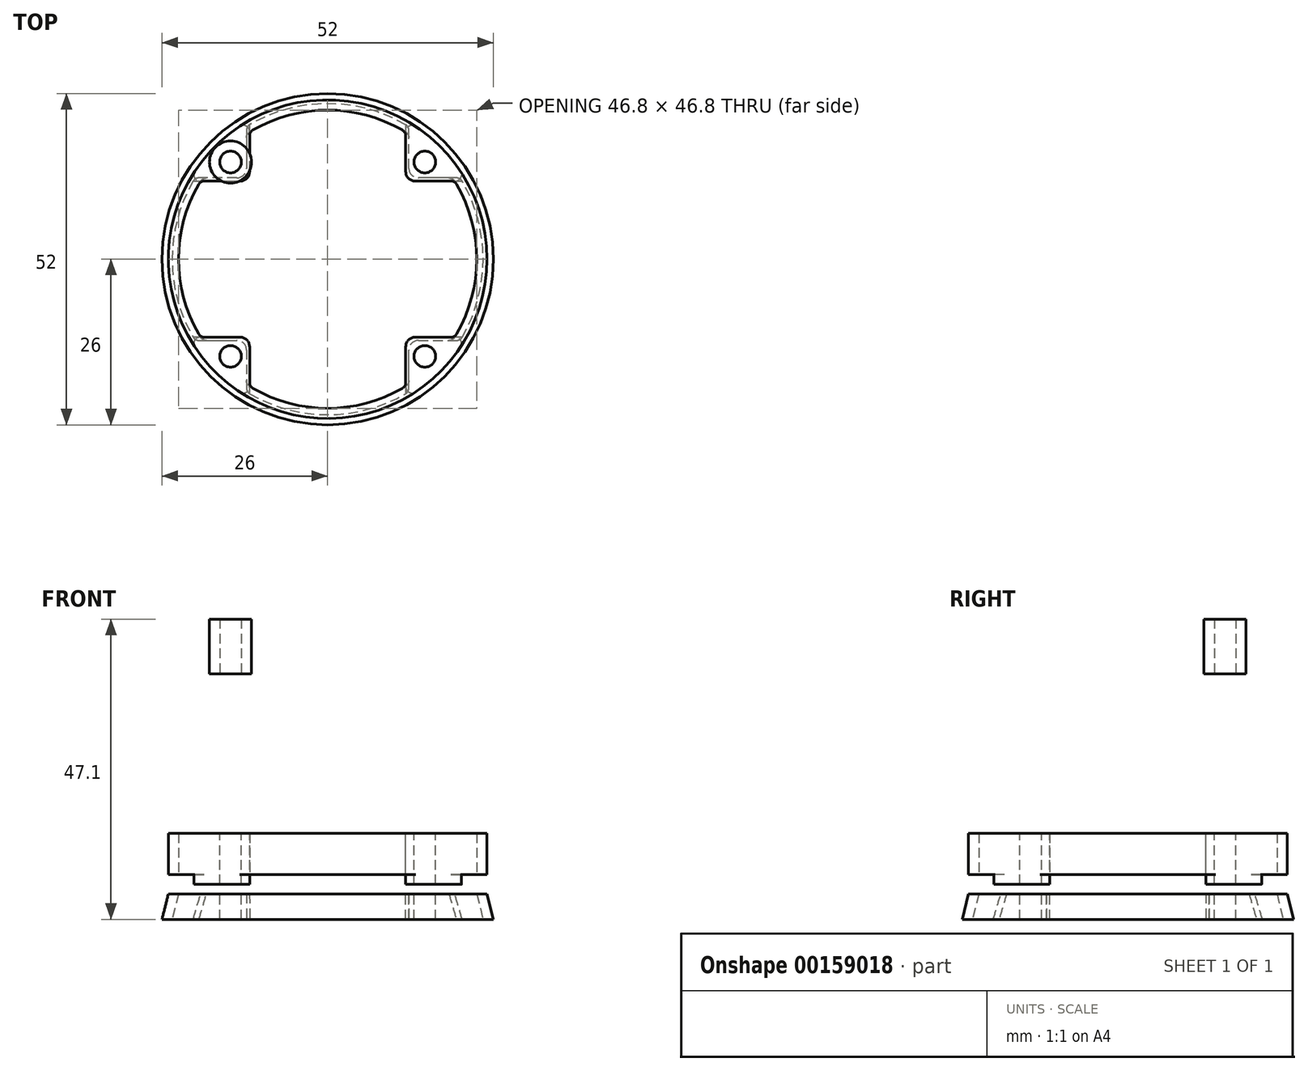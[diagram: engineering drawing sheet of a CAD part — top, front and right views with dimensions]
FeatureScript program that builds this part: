
annotation { "Feature Type Name" : "Feature", "Feature Type Description" : "" }
export const myFeature = defineFeature(function(context is Context, id is Id, definition is map)
    precondition{}
    {
        {
            var Q0;
            Q0=qCreatedBy(makeId("Top.planeOp"),FACE);
            var sketch = newSketch(context, id + "F0", { "sketchPlane" : qUnion([Q0])});
            skCircle(sketch, "E0", {"center": v(0, 0) * mm, "radius": 26 * mm});
            skLineSegment(sketch, "E1.bottom", {"start": v(-16.75, 17.75) * mm, "end": v(16.75, 17.75) * mm, "construction": true});
            skLineSegment(sketch, "E1.top", {"start": v(-16.75, -17.75) * mm, "end": v(16.75, -17.75) * mm, "construction": true});
            skLineSegment(sketch, "E1.left", {"start": v(-18.75, 15.75) * mm, "end": v(-18.75, -15.75) * mm, "construction": true});
            skLineSegment(sketch, "E1.right", {"start": v(18.75, 15.75) * mm, "end": v(18.75, -15.75) * mm, "construction": true});
            skPoint(sketch, "E2.visualSharp", {"position": v(-18.75, 17.75) * mm});
            skArc(sketch, "E2.filletArc", {"start": v(-16.75, 17.75) * mm, "mid": v(-18.16, 17.16) * mm, "end": v(-18.75, 15.75) * mm, "construction": true});
            skPoint(sketch, "E3.visualSharp", {"position": v(18.75, 17.75) * mm});
            skArc(sketch, "E3.filletArc", {"start": v(18.75, 15.75) * mm, "mid": v(18.16, 17.16) * mm, "end": v(16.75, 17.75) * mm, "construction": true});
            skPoint(sketch, "E4.visualSharp", {"position": v(18.75, -17.75) * mm});
            skArc(sketch, "E4.filletArc", {"start": v(16.75, -17.75) * mm, "mid": v(18.16, -17.16) * mm, "end": v(18.75, -15.75) * mm, "construction": true});
            skPoint(sketch, "E5.visualSharp", {"position": v(-18.75, -17.75) * mm});
            skArc(sketch, "E5.filletArc", {"start": v(-18.75, -15.75) * mm, "mid": v(-18.16, -17.16) * mm, "end": v(-16.75, -17.75) * mm, "construction": true});
            skSolve(sketch);
        }
        {
            var Q0;
            Q0 = qSketchRegion(id + "F0", true);
            extrude(context, id + "F1", {"entities" : qUnion([Q0]), "oppositeDirection" : true, "depth" : 4 * mm});
        }
        {
            var Q0;
            Q0=qCreatedBy(makeId("Front.planeOp"),FACE);
            var sketch = newSketch(context, id + "F2", { "sketchPlane" : qUnion([Q0])});
            skLineSegment(sketch, "E6", {"start": v(0, 0) * mm, "end": v(-23.4, 0) * mm});
            skLineSegment(sketch, "E7", {"start": v(-23.4, 0) * mm, "end": v(-24.9, -6) * mm});
            skLineSegment(sketch, "E8", {"start": v(-24.9, -6) * mm, "end": v(0, -6) * mm});
            skLineSegment(sketch, "E9", {"start": v(0, -6) * mm, "end": v(0, 0) * mm});
            skPoint(sketch, "E10", {"position": v(-24.4, -4) * mm});
            skPoint(sketch, "E11", {"position": v(0, -4) * mm});
            skLineSegment(sketch, "E12", {"start": v(0, 0) * mm, "end": v(0, -15.07) * mm, "construction": true});
            skPoint(sketch, "E12.endSnap0", {"position": v(0, -3) * mm});
            skSolve(sketch);
        }
        {
            var Q0;
            Q0 = qSketchRegion(id + "F2", true);
            var Q1;
            Q1=sQuery(id+"F2.wireOp",EDGE,"E12");
            revolve(context, id + "F3", {"operationType" : NewBodyOperationType.REMOVE, "entities" : qUnion([Q0]), "axis" : qUnion([Q1]), "revolveType" : RevolveType.FULL, "oppositeDirection" : true});
        }
        {
            var Q0;
            Q0=makeQuery(id+"F1.opExtrude","CAP_FACE",FACE,{"disambiguationData":[OSD([sQuery(id+"F0.wireOp",EDGE,"E0")])],"isStart":false});
            var sketch = newSketch(context, id + "F4", { "sketchPlane" : qUnion([Q0])});
            skLineSegment(sketch, "E13.bottom", {"start": v(-15.25, 15.25) * mm, "end": v(15.25, 15.25) * mm, "construction": true});
            skLineSegment(sketch, "E13.top", {"start": v(-15.25, -15.25) * mm, "end": v(15.25, -15.25) * mm, "construction": true});
            skLineSegment(sketch, "E13.left", {"start": v(-15.25, 15.25) * mm, "end": v(-15.25, -15.25) * mm, "construction": true});
            skLineSegment(sketch, "E13.right", {"start": v(15.25, 15.25) * mm, "end": v(15.25, -15.25) * mm, "construction": true});
            skPoint(sketch, "E13.middle", {"position": v(0, 0) * mm});
            skLineSegment(sketch, "E14", {"start": v(-20.8, 12.75) * mm, "end": v(-14.25, 12.75) * mm});
            skLineSegment(sketch, "E15", {"start": v(-12.75, 14.25) * mm, "end": v(-12.75, 20.8) * mm});
            skLineSegment(sketch, "E16", {"start": v(12.75, 20.8) * mm, "end": v(12.75, 14.25) * mm});
            skLineSegment(sketch, "E17", {"start": v(14.25, 12.75) * mm, "end": v(20.8, 12.75) * mm});
            skLineSegment(sketch, "E18", {"start": v(20.8, -12.75) * mm, "end": v(14.25, -12.75) * mm});
            skLineSegment(sketch, "E19", {"start": v(12.75, -14.25) * mm, "end": v(12.75, -20.8) * mm});
            skLineSegment(sketch, "E20", {"start": v(-12.75, -20.8) * mm, "end": v(-12.75, -14.25) * mm});
            skLineSegment(sketch, "E21", {"start": v(-14.25, -12.75) * mm, "end": v(-20.8, -12.75) * mm});
            skPoint(sketch, "E22.visualSharp", {"position": v(-12.75, 12.75) * mm});
            skArc(sketch, "E22.filletArc", {"start": v(-14.25, 12.75) * mm, "mid": v(-13.19, 13.19) * mm, "end": v(-12.75, 14.25) * mm});
            skPoint(sketch, "E23.visualSharp", {"position": v(12.75, 12.75) * mm});
            skArc(sketch, "E23.filletArc", {"start": v(12.75, 14.25) * mm, "mid": v(13.19, 13.19) * mm, "end": v(14.25, 12.75) * mm});
            skPoint(sketch, "E24.visualSharp", {"position": v(12.75, -12.75) * mm});
            skArc(sketch, "E24.filletArc", {"start": v(14.25, -12.75) * mm, "mid": v(13.19, -13.19) * mm, "end": v(12.75, -14.25) * mm});
            skPoint(sketch, "E25.visualSharp", {"position": v(-12.75, -12.75) * mm});
            skArc(sketch, "E25.filletArc", {"start": v(-12.75, -14.25) * mm, "mid": v(-13.19, -13.19) * mm, "end": v(-14.25, -12.75) * mm});
            skArc(sketch, "E26", {"start": v(-20.8, -12.75) * mm, "mid": v(-17.25, -17.25) * mm, "end": v(-12.75, -20.8) * mm});
            skArc(sketch, "E27.trimOffspring", {"start": v(-12.75, 20.8) * mm, "mid": v(-17.25, 17.25) * mm, "end": v(-20.8, 12.75) * mm});
            skArc(sketch, "E28.trimOffspring", {"start": v(20.8, 12.75) * mm, "mid": v(17.25, 17.25) * mm, "end": v(12.75, 20.8) * mm});
            skArc(sketch, "E29.trimOffspring", {"start": v(12.75, -20.8) * mm, "mid": v(17.25, -17.25) * mm, "end": v(20.8, -12.75) * mm});
            skSolve(sketch);
        }
        {
            var Q0;
            Q0 = qSketchRegion(id + "F4", true);
            var Q1;
            Q1=makeQuery(id+"F1.opExtrude","CAP_FACE",FACE,{"disambiguationData":[OSD([sQuery(id+"F0.wireOp",EDGE,"E0")])],"isStart":true});
            extrude(context, id + "F5", {"entities" : qUnion([Q0]), "operationType" : NewBodyOperationType.ADD, "endBound" : BoundingType.UP_TO_SURFACE, "oppositeDirection" : true, "endBoundEntityFace" : qUnion([Q1]), "depth" : 25 * mm});
        }
        {
            var Q0;
            {var subQ0=sQuery(id+"F0.wireOp",EDGE,"E0");Q0=makeQuery(id+"F5.boolean.opBoolean","MERGE",FACE,{"derivedFrom":[makeQuery(id+"F1.opExtrude","CAP_FACE",FACE,{"disambiguationData":[OSD([subQ0])],"isStart":true}),makeQuery(id+"F5.opExtrude","CAP_FACE",FACE,{"disambiguationData":[OSD([subQ0]),ownerDisambiguation([makeQuery(id+"F5.opExtrude","SWEPT_BODY",BODY,{"disambiguationData":[OSD([sQuery(id+"F4.wireOp",EDGE,"E14"),sQuery(id+"F4.wireOp",EDGE,"E15"),sQuery(id+"F4.wireOp",EDGE,"E22.filletArc"),sQuery(id+"F4.wireOp",EDGE,"E27.trimOffspring")])]})])],"isStart":false}),makeQuery(id+"F5.opExtrude","CAP_FACE",FACE,{"disambiguationData":[OSD([subQ0]),ownerDisambiguation([makeQuery(id+"F5.opExtrude","SWEPT_BODY",BODY,{"disambiguationData":[OSD([sQuery(id+"F4.wireOp",EDGE,"E16"),sQuery(id+"F4.wireOp",EDGE,"E17"),sQuery(id+"F4.wireOp",EDGE,"E23.filletArc"),sQuery(id+"F4.wireOp",EDGE,"E28.trimOffspring")])]})])],"isStart":false}),makeQuery(id+"F5.opExtrude","CAP_FACE",FACE,{"disambiguationData":[OSD([subQ0]),ownerDisambiguation([makeQuery(id+"F5.opExtrude","SWEPT_BODY",BODY,{"disambiguationData":[OSD([sQuery(id+"F4.wireOp",EDGE,"E18"),sQuery(id+"F4.wireOp",EDGE,"E19"),sQuery(id+"F4.wireOp",EDGE,"E24.filletArc"),sQuery(id+"F4.wireOp",EDGE,"E29.trimOffspring")])]})])],"isStart":false}),makeQuery(id+"F5.opExtrude","CAP_FACE",FACE,{"disambiguationData":[OSD([subQ0]),ownerDisambiguation([makeQuery(id+"F5.opExtrude","SWEPT_BODY",BODY,{"disambiguationData":[OSD([sQuery(id+"F4.wireOp",EDGE,"E20"),sQuery(id+"F4.wireOp",EDGE,"E21"),sQuery(id+"F4.wireOp",EDGE,"E25.filletArc"),sQuery(id+"F4.wireOp",EDGE,"E26")])]})])],"isStart":false})]});}
            var sketch = newSketch(context, id + "F6", { "sketchPlane" : qUnion([Q0])});
            skLineSegment(sketch, "E30.bottom", {"start": v(-15.25, 15.25) * mm, "end": v(15.25, 15.25) * mm, "construction": true});
            skLineSegment(sketch, "E30.top", {"start": v(-15.25, -15.25) * mm, "end": v(15.25, -15.25) * mm, "construction": true});
            skLineSegment(sketch, "E30.left", {"start": v(-15.25, 15.25) * mm, "end": v(-15.25, -15.25) * mm, "construction": true});
            skLineSegment(sketch, "E30.right", {"start": v(15.25, 15.25) * mm, "end": v(15.25, -15.25) * mm, "construction": true});
            skPoint(sketch, "E30.middle", {"position": v(0, 0) * mm});
            skCircle(sketch, "E31", {"center": v(-15.25, 15.25) * mm, "radius": 1.7 * mm});
            skCircle(sketch, "E32", {"center": v(15.25, 15.25) * mm, "radius": 1.7 * mm});
            skCircle(sketch, "E33", {"center": v(15.25, -15.25) * mm, "radius": 1.7 * mm});
            skCircle(sketch, "E34", {"center": v(-15.25, -15.25) * mm, "radius": 1.7 * mm});
            skSolve(sketch);
        }
        {
            var Q0;
            Q0 = qSketchRegion(id + "F6", true);
            extrude(context, id + "F7", {"entities" : qUnion([Q0]), "operationType" : NewBodyOperationType.REMOVE, "oppositeDirection" : true, "depth" : 25 * mm});
        }
        {
            var Q0;
            Q0=qCreatedBy(makeId("Front.planeOp"),FACE);
            var sketch = newSketch(context, id + "F8", { "sketchPlane" : qUnion([Q0])});
            skLineSegment(sketch, "E35", {"start": v(-26, -4) * mm, "end": v(-25, 0) * mm});
            skLineSegment(sketch, "E36", {"start": v(-25, 0) * mm, "end": v(-25, 4) * mm});
            skLineSegment(sketch, "E37", {"start": v(-25, 4) * mm, "end": v(-29.01, 4) * mm});
            skLineSegment(sketch, "E38", {"start": v(-29.01, 4) * mm, "end": v(-29.01, -4) * mm});
            skLineSegment(sketch, "E39", {"start": v(-29.01, -4) * mm, "end": v(-26, -4) * mm});
            skLineSegment(sketch, "E40", {"start": v(0, 0) * mm, "end": v(0, -9.03) * mm, "construction": true});
            skSolve(sketch);
        }
        {
            var Q0;
            Q0 = qSketchRegion(id + "F8", true);
            var Q1;
            Q1=sQuery(id+"F8.wireOp",EDGE,"E40");
            revolve(context, id + "F9", {"operationType" : NewBodyOperationType.REMOVE, "entities" : qUnion([Q0]), "axis" : qUnion([Q1]), "revolveType" : RevolveType.FULL, "oppositeDirection" : true});
        }
        {
            var Q0;
            Q0=makeQuery(id+"F5.boolean.opBoolean","INTERSECT",EDGE,{"derivedFrom":[makeQuery(id+"F3.boolean.opBoolean","COPY",FACE,{"derivedFrom":makeQuery(id+"F3.opRevolve","SWEPT_FACE",FACE,{"disambiguationData":[OSD([sQuery(id+"F2.wireOp",EDGE,"E7")])]})}),makeQuery(id+"F5.opExtrude","SWEPT_FACE",FACE,{"disambiguationData":[OSD([sQuery(id+"F4.wireOp",EDGE,"E21")])]})]});
            var Q1;
            Q1=makeQuery(id+"F5.boolean.opBoolean","INTERSECT",EDGE,{"derivedFrom":[makeQuery(id+"F3.boolean.opBoolean","COPY",FACE,{"derivedFrom":makeQuery(id+"F3.opRevolve","SWEPT_FACE",FACE,{"disambiguationData":[OSD([sQuery(id+"F2.wireOp",EDGE,"E7")])]})}),makeQuery(id+"F5.opExtrude","SWEPT_FACE",FACE,{"disambiguationData":[OSD([sQuery(id+"F4.wireOp",EDGE,"E14")])]})]});
            var Q2;
            Q2=makeQuery(id+"F5.boolean.opBoolean","INTERSECT",EDGE,{"derivedFrom":[makeQuery(id+"F3.boolean.opBoolean","COPY",FACE,{"derivedFrom":makeQuery(id+"F3.opRevolve","SWEPT_FACE",FACE,{"disambiguationData":[OSD([sQuery(id+"F2.wireOp",EDGE,"E7")])]})}),makeQuery(id+"F5.opExtrude","SWEPT_FACE",FACE,{"disambiguationData":[OSD([sQuery(id+"F4.wireOp",EDGE,"E15")])]})]});
            var Q3;
            Q3=makeQuery(id+"F5.boolean.opBoolean","INTERSECT",EDGE,{"derivedFrom":[makeQuery(id+"F3.boolean.opBoolean","COPY",FACE,{"derivedFrom":makeQuery(id+"F3.opRevolve","SWEPT_FACE",FACE,{"disambiguationData":[OSD([sQuery(id+"F2.wireOp",EDGE,"E7")])]})}),makeQuery(id+"F5.opExtrude","SWEPT_FACE",FACE,{"disambiguationData":[OSD([sQuery(id+"F4.wireOp",EDGE,"E16")])]})]});
            var Q4;
            Q4=makeQuery(id+"F5.boolean.opBoolean","INTERSECT",EDGE,{"derivedFrom":[makeQuery(id+"F3.boolean.opBoolean","COPY",FACE,{"derivedFrom":makeQuery(id+"F3.opRevolve","SWEPT_FACE",FACE,{"disambiguationData":[OSD([sQuery(id+"F2.wireOp",EDGE,"E7")])]})}),makeQuery(id+"F5.opExtrude","SWEPT_FACE",FACE,{"disambiguationData":[OSD([sQuery(id+"F4.wireOp",EDGE,"E17")])]})]});
            var Q5;
            Q5=makeQuery(id+"F5.boolean.opBoolean","INTERSECT",EDGE,{"derivedFrom":[makeQuery(id+"F3.boolean.opBoolean","COPY",FACE,{"derivedFrom":makeQuery(id+"F3.opRevolve","SWEPT_FACE",FACE,{"disambiguationData":[OSD([sQuery(id+"F2.wireOp",EDGE,"E7")])]})}),makeQuery(id+"F5.opExtrude","SWEPT_FACE",FACE,{"disambiguationData":[OSD([sQuery(id+"F4.wireOp",EDGE,"E18")])]})]});
            var Q6;
            Q6=makeQuery(id+"F5.boolean.opBoolean","INTERSECT",EDGE,{"derivedFrom":[makeQuery(id+"F3.boolean.opBoolean","COPY",FACE,{"derivedFrom":makeQuery(id+"F3.opRevolve","SWEPT_FACE",FACE,{"disambiguationData":[OSD([sQuery(id+"F2.wireOp",EDGE,"E7")])]})}),makeQuery(id+"F5.opExtrude","SWEPT_FACE",FACE,{"disambiguationData":[OSD([sQuery(id+"F4.wireOp",EDGE,"E19")])]})]});
            var Q7;
            Q7=makeQuery(id+"F5.boolean.opBoolean","INTERSECT",EDGE,{"derivedFrom":[makeQuery(id+"F3.boolean.opBoolean","COPY",FACE,{"derivedFrom":makeQuery(id+"F3.opRevolve","SWEPT_FACE",FACE,{"disambiguationData":[OSD([sQuery(id+"F2.wireOp",EDGE,"E7")])]})}),makeQuery(id+"F5.opExtrude","SWEPT_FACE",FACE,{"disambiguationData":[OSD([sQuery(id+"F4.wireOp",EDGE,"E20")])]})]});
            fillet(context, id + "F10", {"entities" : qUnion([Q0, Q1, Q2, Q3, Q4, Q5, Q6, Q7]), "radius" : 1 * mm, "tangentPropagation" : true, "allowEdgeOverflow" : false});
        }
        {
            var Q0;
            {var subQ0=sQuery(id+"F0.wireOp",EDGE,"E0");Q0=makeQuery(id+"F5.boolean.opBoolean","MERGE",FACE,{"derivedFrom":[makeQuery(id+"F1.opExtrude","CAP_FACE",FACE,{"disambiguationData":[OSD([subQ0])],"isStart":true}),makeQuery(id+"F5.opExtrude","CAP_FACE",FACE,{"disambiguationData":[OSD([subQ0]),ownerDisambiguation([makeQuery(id+"F5.opExtrude","SWEPT_BODY",BODY,{"disambiguationData":[OSD([sQuery(id+"F4.wireOp",EDGE,"E14"),sQuery(id+"F4.wireOp",EDGE,"E15"),sQuery(id+"F4.wireOp",EDGE,"E22.filletArc"),sQuery(id+"F4.wireOp",EDGE,"E27.trimOffspring")])]})])],"isStart":false}),makeQuery(id+"F5.opExtrude","CAP_FACE",FACE,{"disambiguationData":[OSD([subQ0]),ownerDisambiguation([makeQuery(id+"F5.opExtrude","SWEPT_BODY",BODY,{"disambiguationData":[OSD([sQuery(id+"F4.wireOp",EDGE,"E16"),sQuery(id+"F4.wireOp",EDGE,"E17"),sQuery(id+"F4.wireOp",EDGE,"E23.filletArc"),sQuery(id+"F4.wireOp",EDGE,"E28.trimOffspring")])]})])],"isStart":false}),makeQuery(id+"F5.opExtrude","CAP_FACE",FACE,{"disambiguationData":[OSD([subQ0]),ownerDisambiguation([makeQuery(id+"F5.opExtrude","SWEPT_BODY",BODY,{"disambiguationData":[OSD([sQuery(id+"F4.wireOp",EDGE,"E18"),sQuery(id+"F4.wireOp",EDGE,"E19"),sQuery(id+"F4.wireOp",EDGE,"E24.filletArc"),sQuery(id+"F4.wireOp",EDGE,"E29.trimOffspring")])]})])],"isStart":false}),makeQuery(id+"F5.opExtrude","CAP_FACE",FACE,{"disambiguationData":[OSD([subQ0]),ownerDisambiguation([makeQuery(id+"F5.opExtrude","SWEPT_BODY",BODY,{"disambiguationData":[OSD([sQuery(id+"F4.wireOp",EDGE,"E20"),sQuery(id+"F4.wireOp",EDGE,"E21"),sQuery(id+"F4.wireOp",EDGE,"E25.filletArc"),sQuery(id+"F4.wireOp",EDGE,"E26")])]})])],"isStart":false})]});}
            cPlane(context, id + "F11", {"entities" : qUnion([Q0]), "cplaneType" : CPlaneType.OFFSET, "offset" : 3 * mm, "width" : 150 * mm, "height" : 150 * mm});
        }
        {
            var Q0;
            Q0=qCreatedBy(id+"F11.planeOp",FACE);
            var sketch = newSketch(context, id + "F12", { "sketchPlane" : qUnion([Q0])});
            skCircle(sketch, "E41", {"center": v(0, 0) * mm, "radius": 25 * mm});
            skCircle(sketch, "E42", {"center": v(0, 0) * mm, "radius": 23.4 * mm});
            skSolve(sketch);
        }
        {
            var Q0;
            Q0 = qSketchRegion(id + "F12", true);
            extrude(context, id + "F13", {"entities" : qUnion([Q0]), "depth" : 6.5 * mm});
        }
        {
            var Q0;
            Q0=makeQuery(id+"F13.opExtrude","CAP_FACE",FACE,{"disambiguationData":[OSD([sQuery(id+"F12.wireOp",EDGE,"E41"),sQuery(id+"F12.wireOp",EDGE,"E42")])],"isStart":false});
            var sketch = newSketch(context, id + "F14", { "sketchPlane" : qUnion([Q0])});
            skArc(sketch, "E43", {"start": v(-21.8, -12.25) * mm, "mid": v(-17.68, -17.68) * mm, "end": v(-12.25, -21.8) * mm});
            skLineSegment(sketch, "E44", {"start": v(-21.8, 12.25) * mm, "end": v(-13.75, 12.25) * mm});
            skLineSegment(sketch, "E45", {"start": v(-12.25, 13.75) * mm, "end": v(-12.25, 21.8) * mm});
            skLineSegment(sketch, "E46", {"start": v(12.25, 21.8) * mm, "end": v(12.25, 13.75) * mm});
            skLineSegment(sketch, "E47", {"start": v(13.75, 12.25) * mm, "end": v(21.8, 12.25) * mm});
            skLineSegment(sketch, "E48", {"start": v(21.8, -12.25) * mm, "end": v(13.75, -12.25) * mm});
            skLineSegment(sketch, "E49", {"start": v(12.25, -13.75) * mm, "end": v(12.25, -21.8) * mm});
            skLineSegment(sketch, "E50", {"start": v(-21.8, -12.25) * mm, "end": v(-13.75, -12.25) * mm});
            skLineSegment(sketch, "E51", {"start": v(-12.25, -13.75) * mm, "end": v(-12.25, -21.8) * mm});
            skArc(sketch, "E52.trimOffspring", {"start": v(-12.25, 21.8) * mm, "mid": v(-17.68, 17.68) * mm, "end": v(-21.8, 12.25) * mm});
            skArc(sketch, "E53.trimOffspring", {"start": v(21.8, 12.25) * mm, "mid": v(17.68, 17.68) * mm, "end": v(12.25, 21.8) * mm});
            skArc(sketch, "E54.trimOffspring", {"start": v(12.25, -21.8) * mm, "mid": v(17.68, -17.68) * mm, "end": v(21.8, -12.25) * mm});
            skCircle(sketch, "E55.0", {"center": v(-15.25, 15.25) * mm, "radius": 1.7 * mm});
            skCircle(sketch, "E55.1", {"center": v(-15.25, -15.25) * mm, "radius": 1.7 * mm});
            skCircle(sketch, "E55.2", {"center": v(15.25, -15.25) * mm, "radius": 1.7 * mm});
            skCircle(sketch, "E55.3", {"center": v(15.25, 15.25) * mm, "radius": 1.7 * mm});
            skPoint(sketch, "E56.visualSharp", {"position": v(-12.25, 12.25) * mm});
            skArc(sketch, "E56.filletArc", {"start": v(-13.75, 12.25) * mm, "mid": v(-12.69, 12.69) * mm, "end": v(-12.25, 13.75) * mm});
            skPoint(sketch, "E57.visualSharp", {"position": v(12.25, 12.25) * mm});
            skArc(sketch, "E57.filletArc", {"start": v(12.25, 13.75) * mm, "mid": v(12.69, 12.69) * mm, "end": v(13.75, 12.25) * mm});
            skPoint(sketch, "E58.visualSharp", {"position": v(12.25, -12.25) * mm});
            skArc(sketch, "E58.filletArc", {"start": v(13.75, -12.25) * mm, "mid": v(12.69, -12.69) * mm, "end": v(12.25, -13.75) * mm});
            skPoint(sketch, "E59.visualSharp", {"position": v(-12.25, -12.25) * mm});
            skArc(sketch, "E59.filletArc", {"start": v(-12.25, -13.75) * mm, "mid": v(-12.69, -12.69) * mm, "end": v(-13.75, -12.25) * mm});
            skSolve(sketch);
        }
        {
            var Q0;
            Q0 = qSketchRegion(id + "F14", true);
            extrude(context, id + "F15", {"entities" : qUnion([Q0]), "operationType" : NewBodyOperationType.ADD, "oppositeDirection" : true, "depth" : 8 * mm});
        }
        {
            var Q0;
            Q0=makeQuery(id+"F15.boolean.opBoolean","INTERSECT",EDGE,{"derivedFrom":[makeQuery(id+"F13.opExtrude","SWEPT_FACE",FACE,{"disambiguationData":[OSD([sQuery(id+"F12.wireOp",EDGE,"E42")])]}),makeQuery(id+"F15.opExtrude","SWEPT_FACE",FACE,{"disambiguationData":[OSD([sQuery(id+"F14.wireOp",EDGE,"E44")])]})]});
            var Q1;
            Q1=makeQuery(id+"F15.boolean.opBoolean","INTERSECT",EDGE,{"derivedFrom":[makeQuery(id+"F13.opExtrude","SWEPT_FACE",FACE,{"disambiguationData":[OSD([sQuery(id+"F12.wireOp",EDGE,"E42")])]}),makeQuery(id+"F15.opExtrude","SWEPT_FACE",FACE,{"disambiguationData":[OSD([sQuery(id+"F14.wireOp",EDGE,"E45")])]})]});
            var Q2;
            Q2=makeQuery(id+"F15.boolean.opBoolean","INTERSECT",EDGE,{"derivedFrom":[makeQuery(id+"F13.opExtrude","SWEPT_FACE",FACE,{"disambiguationData":[OSD([sQuery(id+"F12.wireOp",EDGE,"E42")])]}),makeQuery(id+"F15.opExtrude","SWEPT_FACE",FACE,{"disambiguationData":[OSD([sQuery(id+"F14.wireOp",EDGE,"E46")])]})]});
            var Q3;
            Q3=makeQuery(id+"F15.boolean.opBoolean","INTERSECT",EDGE,{"derivedFrom":[makeQuery(id+"F13.opExtrude","SWEPT_FACE",FACE,{"disambiguationData":[OSD([sQuery(id+"F12.wireOp",EDGE,"E42")])]}),makeQuery(id+"F15.opExtrude","SWEPT_FACE",FACE,{"disambiguationData":[OSD([sQuery(id+"F14.wireOp",EDGE,"E47")])]})]});
            var Q4;
            Q4=makeQuery(id+"F15.boolean.opBoolean","INTERSECT",EDGE,{"derivedFrom":[makeQuery(id+"F13.opExtrude","SWEPT_FACE",FACE,{"disambiguationData":[OSD([sQuery(id+"F12.wireOp",EDGE,"E42")])]}),makeQuery(id+"F15.opExtrude","SWEPT_FACE",FACE,{"disambiguationData":[OSD([sQuery(id+"F14.wireOp",EDGE,"E48")])]})]});
            var Q5;
            Q5=makeQuery(id+"F15.boolean.opBoolean","INTERSECT",EDGE,{"derivedFrom":[makeQuery(id+"F13.opExtrude","SWEPT_FACE",FACE,{"disambiguationData":[OSD([sQuery(id+"F12.wireOp",EDGE,"E42")])]}),makeQuery(id+"F15.opExtrude","SWEPT_FACE",FACE,{"disambiguationData":[OSD([sQuery(id+"F14.wireOp",EDGE,"E49")])]})]});
            var Q6;
            Q6=makeQuery(id+"F15.boolean.opBoolean","INTERSECT",EDGE,{"derivedFrom":[makeQuery(id+"F13.opExtrude","SWEPT_FACE",FACE,{"disambiguationData":[OSD([sQuery(id+"F12.wireOp",EDGE,"E42")])]}),makeQuery(id+"F15.opExtrude","SWEPT_FACE",FACE,{"disambiguationData":[OSD([sQuery(id+"F14.wireOp",EDGE,"E51")])]})]});
            var Q7;
            Q7=makeQuery(id+"F15.boolean.opBoolean","INTERSECT",EDGE,{"derivedFrom":[makeQuery(id+"F13.opExtrude","SWEPT_FACE",FACE,{"disambiguationData":[OSD([sQuery(id+"F12.wireOp",EDGE,"E42")])]}),makeQuery(id+"F15.opExtrude","SWEPT_FACE",FACE,{"disambiguationData":[OSD([sQuery(id+"F14.wireOp",EDGE,"E50")])]})]});
            var Q8;
            Q8=makeQuery(id+"F15.opExtrude","SWEPT_EDGE",EDGE,{"disambiguationData":[OSD([sQuery(id+"F12.wireOp",EDGE,"E41"),sQuery(id+"F14.wireOp",EDGE,"E43"),sQuery(id+"F14.wireOp",EDGE,"E50")])]});
            var Q9;
            Q9=makeQuery(id+"F15.opExtrude","SWEPT_EDGE",EDGE,{"disambiguationData":[OSD([sQuery(id+"F12.wireOp",EDGE,"E41"),sQuery(id+"F14.wireOp",EDGE,"E44"),sQuery(id+"F14.wireOp",EDGE,"E52.trimOffspring")])]});
            var Q10;
            Q10=makeQuery(id+"F15.opExtrude","SWEPT_EDGE",EDGE,{"disambiguationData":[OSD([sQuery(id+"F12.wireOp",EDGE,"E41"),sQuery(id+"F14.wireOp",EDGE,"E43"),sQuery(id+"F14.wireOp",EDGE,"E51")])]});
            var Q11;
            Q11=makeQuery(id+"F15.opExtrude","SWEPT_EDGE",EDGE,{"disambiguationData":[OSD([sQuery(id+"F12.wireOp",EDGE,"E41"),sQuery(id+"F14.wireOp",EDGE,"E49"),sQuery(id+"F14.wireOp",EDGE,"E54.trimOffspring")])]});
            var Q12;
            Q12=makeQuery(id+"F15.opExtrude","SWEPT_EDGE",EDGE,{"disambiguationData":[OSD([sQuery(id+"F12.wireOp",EDGE,"E41"),sQuery(id+"F14.wireOp",EDGE,"E48"),sQuery(id+"F14.wireOp",EDGE,"E54.trimOffspring")])]});
            var Q13;
            Q13=makeQuery(id+"F15.opExtrude","SWEPT_EDGE",EDGE,{"disambiguationData":[OSD([sQuery(id+"F12.wireOp",EDGE,"E41"),sQuery(id+"F14.wireOp",EDGE,"E47"),sQuery(id+"F14.wireOp",EDGE,"E53.trimOffspring")])]});
            var Q14;
            Q14=makeQuery(id+"F15.opExtrude","SWEPT_EDGE",EDGE,{"disambiguationData":[OSD([sQuery(id+"F12.wireOp",EDGE,"E41"),sQuery(id+"F14.wireOp",EDGE,"E46"),sQuery(id+"F14.wireOp",EDGE,"E53.trimOffspring")])]});
            var Q15;
            Q15=makeQuery(id+"F15.opExtrude","SWEPT_EDGE",EDGE,{"disambiguationData":[OSD([sQuery(id+"F12.wireOp",EDGE,"E41"),sQuery(id+"F14.wireOp",EDGE,"E45"),sQuery(id+"F14.wireOp",EDGE,"E52.trimOffspring")])]});
            fillet(context, id + "F16", {"entities" : qUnion([Q0, Q1, Q2, Q3, Q4, Q5, Q6, Q7, Q8, Q9, Q10, Q11, Q12, Q13, Q14, Q15]), "radius" : 1 * mm, "tangentPropagation" : true, "allowEdgeOverflow" : false});
        }
        {
            var Q0;
            Q0=makeQuery(id+"F15.boolean.opBoolean","MERGE",FACE,{"derivedFrom":[makeQuery(id+"F13.opExtrude","CAP_FACE",FACE,{"disambiguationData":[OSD([sQuery(id+"F12.wireOp",EDGE,"E41"),sQuery(id+"F12.wireOp",EDGE,"E42")])],"isStart":false}),makeQuery(id+"F15.opExtrude","CAP_FACE",FACE,{"disambiguationData":[OSD([sQuery(id+"F14.wireOp",EDGE,"E43"),sQuery(id+"F14.wireOp",EDGE,"E50"),sQuery(id+"F14.wireOp",EDGE,"E51"),sQuery(id+"F14.wireOp",EDGE,"E55.1"),sQuery(id+"F14.wireOp",EDGE,"E59.filletArc")])],"isStart":true}),makeQuery(id+"F15.opExtrude","CAP_FACE",FACE,{"disambiguationData":[OSD([sQuery(id+"F14.wireOp",EDGE,"E44"),sQuery(id+"F14.wireOp",EDGE,"E45"),sQuery(id+"F14.wireOp",EDGE,"E52.trimOffspring"),sQuery(id+"F14.wireOp",EDGE,"E55.0"),sQuery(id+"F14.wireOp",EDGE,"E56.filletArc")])],"isStart":true}),makeQuery(id+"F15.opExtrude","CAP_FACE",FACE,{"disambiguationData":[OSD([sQuery(id+"F14.wireOp",EDGE,"E46"),sQuery(id+"F14.wireOp",EDGE,"E47"),sQuery(id+"F14.wireOp",EDGE,"E53.trimOffspring"),sQuery(id+"F14.wireOp",EDGE,"E55.3"),sQuery(id+"F14.wireOp",EDGE,"E57.filletArc")])],"isStart":true}),makeQuery(id+"F15.opExtrude","CAP_FACE",FACE,{"disambiguationData":[OSD([sQuery(id+"F14.wireOp",EDGE,"E48"),sQuery(id+"F14.wireOp",EDGE,"E49"),sQuery(id+"F14.wireOp",EDGE,"E54.trimOffspring"),sQuery(id+"F14.wireOp",EDGE,"E55.2"),sQuery(id+"F14.wireOp",EDGE,"E58.filletArc")])],"isStart":true})]});
            cPlane(context, id + "F17", {"entities" : qUnion([Q0]), "cplaneType" : CPlaneType.OFFSET, "offset" : 25 * mm, "width" : 150 * mm, "height" : 150 * mm});
        }
        {
            var Q0;
            Q0=qCreatedBy(id+"F17.planeOp",FACE);
            var sketch = newSketch(context, id + "F18", { "sketchPlane" : qUnion([Q0])});
            skCircle(sketch, "E60", {"center": v(-15.25, 15.25) * mm, "radius": 1.7 * mm});
            skCircle(sketch, "E61", {"center": v(-15.25, 15.25) * mm, "radius": 3.3 * mm});
            skSolve(sketch);
        }
        {
            var Q0;
            Q0 = qSketchRegion(id + "F18", true);
            extrude(context, id + "F19", {"entities" : qUnion([Q0]), "depth" : 8.6 * mm});
        }
    });
